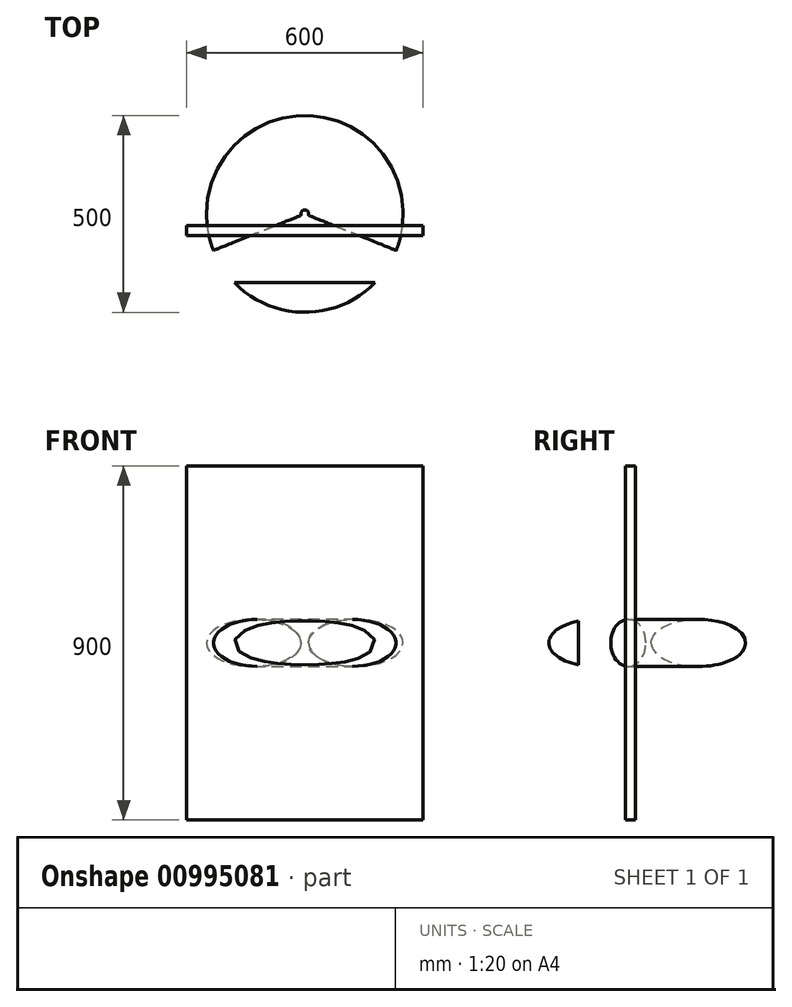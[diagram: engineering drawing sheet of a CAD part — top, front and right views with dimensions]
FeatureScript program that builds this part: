
annotation { "Feature Type Name" : "Feature", "Feature Type Description" : "" }
export const myFeature = defineFeature(function(context is Context, id is Id, definition is map)
    precondition{}
    {
        {
            var Q0;
            Q0=qCreatedBy(makeId("Front.planeOp"),FACE);
            cPlane(context, id + "F0", {"entities" : qUnion([Q0]), "cplaneType" : CPlaneType.OFFSET, "offset" : 30 * mm, "width" : 150 * mm, "height" : 150 * mm});
        }
        {
            var Q0;
            Q0=qCreatedBy(id+"F0.planeOp",FACE);
            var sketch = newSketch(context, id + "F1", { "sketchPlane" : qUnion([Q0])});
            skLineSegment(sketch, "E0.bottom", {"start": v(300, -450) * mm, "end": v(-300, -450) * mm});
            skLineSegment(sketch, "E0.top", {"start": v(300, 450) * mm, "end": v(-300, 450) * mm});
            skLineSegment(sketch, "E0.left", {"start": v(300, -450) * mm, "end": v(300, 450) * mm});
            skLineSegment(sketch, "E0.right", {"start": v(-300, -450) * mm, "end": v(-300, 450) * mm});
            skPoint(sketch, "E0.middle", {"position": v(0, 0) * mm});
            skSolve(sketch);
        }
        {
            var Q0;
            Q0=qCreatedBy(makeId("Front.planeOp"),FACE);
            var sketch = newSketch(context, id + "F2", { "sketchPlane" : qUnion([Q0])});
            skEllipse(sketch, "E1", {"center": v(-130, 0) * mm, "majorRadius": 120 * mm, "minorRadius": 60 * mm, "majorAxis": v(1, 0)});
            skLineSegment(sketch, "E2", {"start": v(0, 102.6) * mm, "end": v(0, -125.8) * mm});
            skSolve(sketch);
        }
        {
            var Q0;
            Q0=makeQuery(id+"F2.imprint","IMPRINT",FACE,{"disambiguationData":[TD([[makeQuery(id+"F2.imprint","IMPRINT",EDGE,{"derivedFrom":sQuery(id+"F2.wireOp",EDGE,"E1")}),1.0]])]});
            var Q1;
            Q1=sQuery(id+"F2.wireOp",EDGE,"E2");
            revolve(context, id + "F3", {"surfaceOperationType" : NewSurfaceOperationType.NEW, "entities" : qUnion([Q0]), "axis" : qUnion([Q1]), "revolveType" : RevolveType.FULL});
        }
        {
            var Q0;
            Q0=qCreatedBy(makeId("Top.planeOp"),FACE);
            var sketch = newSketch(context, id + "F4", { "sketchPlane" : qUnion([Q0])});
            skPoint(sketch, "E3", {"position": v(0, 0) * mm});
            skLineSegment(sketch, "E4", {"start": v(0, 0) * mm, "end": v(0, 0) * mm});
            skPoint(sketch, "E5", {"position": v(-50, -20) * mm});
            skPoint(sketch, "E6", {"position": v(50, -20) * mm});
            skLineSegment(sketch, "E7", {"start": v(0, 0) * mm, "end": v(50, -20) * mm});
            skLineSegment(sketch, "E8", {"start": v(50, -20) * mm, "end": v(437.23, -174.9) * mm});
            skLineSegment(sketch, "E9", {"start": v(0, 0) * mm, "end": v(-50, -20) * mm});
            skLineSegment(sketch, "E10", {"start": v(0, 0) * mm, "end": v(-437.23, -174.9) * mm});
            skLineSegment(sketch, "E11", {"start": v(-437.23, -174.9) * mm, "end": v(437.23, -174.9) * mm});
            skSolve(sketch);
        }
        {
            var Q0;
            Q0 = qSketchRegion(id + "F4", true);
            extrude(context, id + "F5", {"entities" : qUnion([Q0]), "operationType" : NewBodyOperationType.REMOVE, "endBound" : BoundingType.SYMMETRIC, "depth" : 172 * mm, "offsetDistance" : 25 * mm});
        }
        {
            var Q0;
            Q0=makeQuery(id+"F1.imprint","IMPRINT",FACE,{"disambiguationData":[TD([[makeQuery(id+"F1.imprint","IMPRINT",EDGE,{"derivedFrom":sQuery(id+"F1.wireOp",EDGE,"E0.bottom")}),-1.0]])]});
            extrude(context, id + "F6", {"entities" : qUnion([Q0]), "depth" : 25 * mm, "offsetDistance" : 25 * mm});
        }
    });
